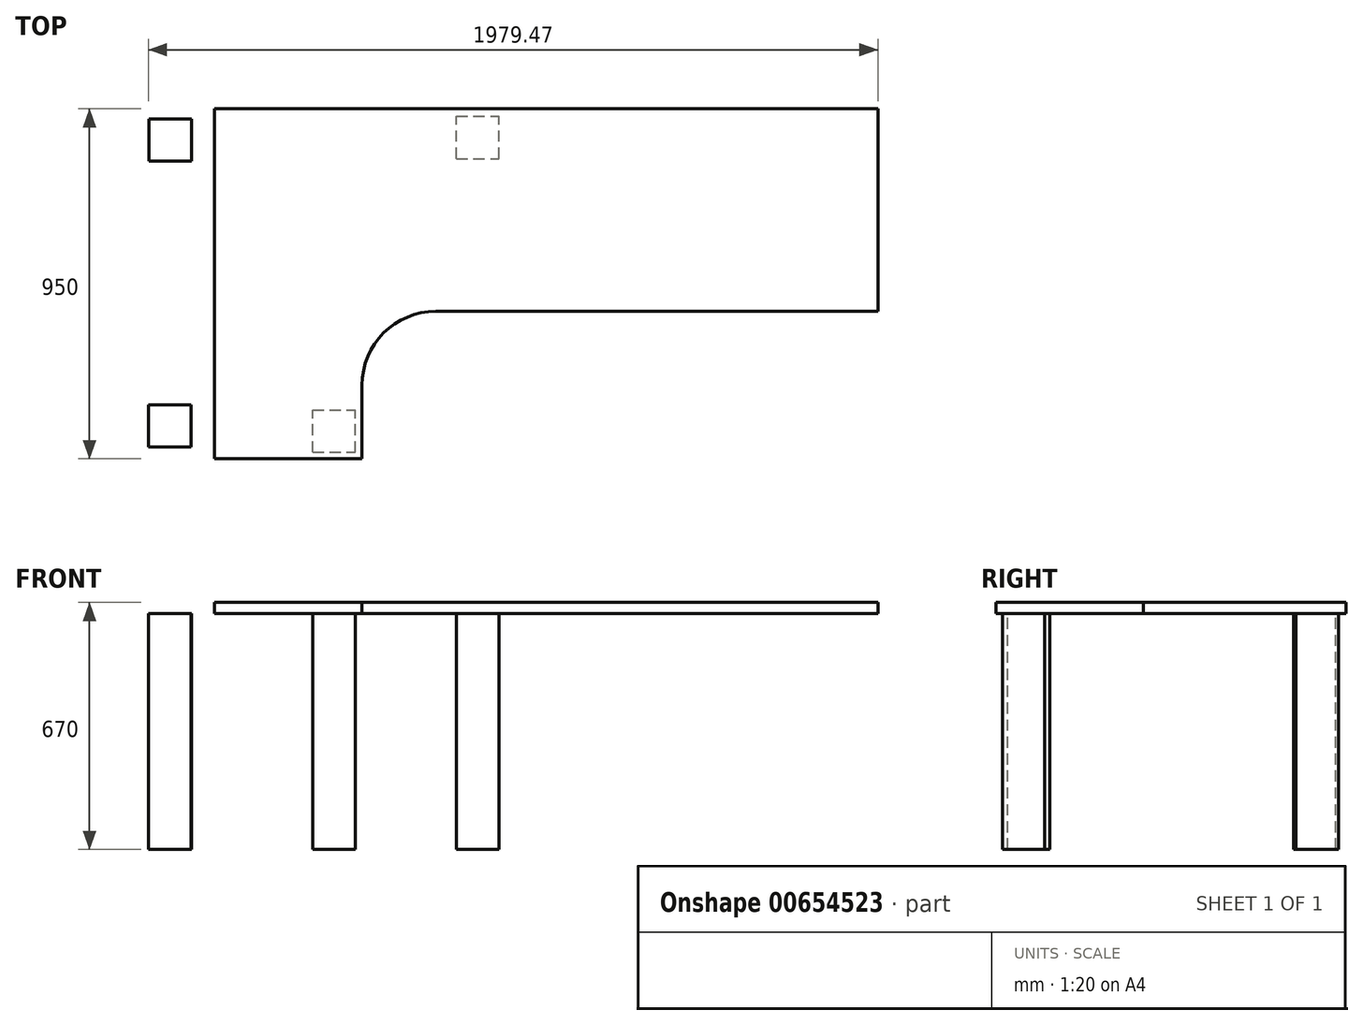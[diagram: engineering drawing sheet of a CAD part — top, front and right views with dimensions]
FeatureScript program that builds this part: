
annotation { "Feature Type Name" : "Feature", "Feature Type Description" : "" }
export const myFeature = defineFeature(function(context is Context, id is Id, definition is map)
    precondition{}
    {
        {
            var Q0;
            Q0=qCreatedBy(makeId("Top.planeOp"),FACE);
            var sketch = newSketch(context, id + "F0", { "sketchPlane" : qUnion([Q0])});
            skLineSegment(sketch, "E0", {"start": v(1558.67, 0) * mm, "end": v(1558.67, 550) * mm});
            skLineSegment(sketch, "E1", {"start": v(1558.67, 550) * mm, "end": v(-241.33, 550) * mm});
            skLineSegment(sketch, "E2", {"start": v(-241.33, 550) * mm, "end": v(-241.33, 0) * mm});
            skLineSegment(sketch, "E3", {"start": v(-241.33, 0) * mm, "end": v(-241.33, -400) * mm});
            skLineSegment(sketch, "E4", {"start": v(-241.33, -400) * mm, "end": v(158.67, -400) * mm});
            skLineSegment(sketch, "E5", {"start": v(158.67, -400) * mm, "end": v(158.67, -200) * mm});
            skLineSegment(sketch, "E6", {"start": v(358.67, 0) * mm, "end": v(1558.67, 0) * mm});
            skPoint(sketch, "E7.visualSharp", {"position": v(158.67, 0) * mm});
            skArc(sketch, "E7.filletArc", {"start": v(358.67, 0) * mm, "mid": v(217.25, -58.58) * mm, "end": v(158.67, -200) * mm});
            skSolve(sketch);
        }
        {
            var Q0;
            Q0 = qSketchRegion(id + "F0", true);
            extrude(context, id + "F1", {"entities" : qUnion([Q0]), "depth" : 30 * mm, "offsetDistance" : 25 * mm});
        }
        {
            var Q0;
            Q0=makeQuery(id+"F1.opExtrude","CAP_FACE",FACE,{"disambiguationData":[OSD([sQuery(id+"F0.wireOp",EDGE,"E0"),sQuery(id+"F0.wireOp",EDGE,"E1"),sQuery(id+"F0.wireOp",EDGE,"E2"),sQuery(id+"F0.wireOp",EDGE,"E3"),sQuery(id+"F0.wireOp",EDGE,"E4"),sQuery(id+"F0.wireOp",EDGE,"E5"),sQuery(id+"F0.wireOp",EDGE,"E6"),sQuery(id+"F0.wireOp",EDGE,"E7.filletArc")])],"isStart":true});
            var sketch = newSketch(context, id + "F2", { "sketchPlane" : qUnion([Q0])});
            skLineSegment(sketch, "E8.bottom", {"start": v(-419.37, -407.81) * mm, "end": v(-304.37, -407.81) * mm});
            skLineSegment(sketch, "E8.top", {"start": v(-419.37, -522.81) * mm, "end": v(-304.37, -522.81) * mm});
            skLineSegment(sketch, "E8.left", {"start": v(-419.37, -407.81) * mm, "end": v(-419.37, -522.81) * mm});
            skLineSegment(sketch, "E8.right", {"start": v(-304.37, -407.81) * mm, "end": v(-304.37, -522.81) * mm});
            skLineSegment(sketch, "E9.bottom", {"start": v(415.07, -414.81) * mm, "end": v(530.07, -414.81) * mm});
            skLineSegment(sketch, "E9.top", {"start": v(415.07, -529.81) * mm, "end": v(530.07, -529.81) * mm});
            skLineSegment(sketch, "E9.left", {"start": v(415.07, -414.81) * mm, "end": v(415.07, -529.81) * mm});
            skLineSegment(sketch, "E9.right", {"start": v(530.07, -414.81) * mm, "end": v(530.07, -529.81) * mm});
            skLineSegment(sketch, "E10.bottom", {"start": v(-420.8, 368.12) * mm, "end": v(-305.8, 368.12) * mm});
            skLineSegment(sketch, "E10.top", {"start": v(-420.8, 253.12) * mm, "end": v(-305.8, 253.12) * mm});
            skLineSegment(sketch, "E10.left", {"start": v(-420.8, 368.12) * mm, "end": v(-420.8, 253.12) * mm});
            skLineSegment(sketch, "E10.right", {"start": v(-305.8, 368.12) * mm, "end": v(-305.8, 253.12) * mm});
            skLineSegment(sketch, "E11.bottom", {"start": v(25, 382.16) * mm, "end": v(140, 382.16) * mm});
            skLineSegment(sketch, "E11.top", {"start": v(25, 267.16) * mm, "end": v(140, 267.16) * mm});
            skLineSegment(sketch, "E11.left", {"start": v(25, 382.16) * mm, "end": v(25, 267.16) * mm});
            skLineSegment(sketch, "E11.right", {"start": v(140, 382.16) * mm, "end": v(140, 267.16) * mm});
            skSolve(sketch);
        }
        {
            var Q0;
            Q0 = qSketchRegion(id + "F2", true);
            extrude(context, id + "F3", {"entities" : qUnion([Q0]), "depth" : 640 * mm, "offsetDistance" : 25 * mm});
        }
    });
